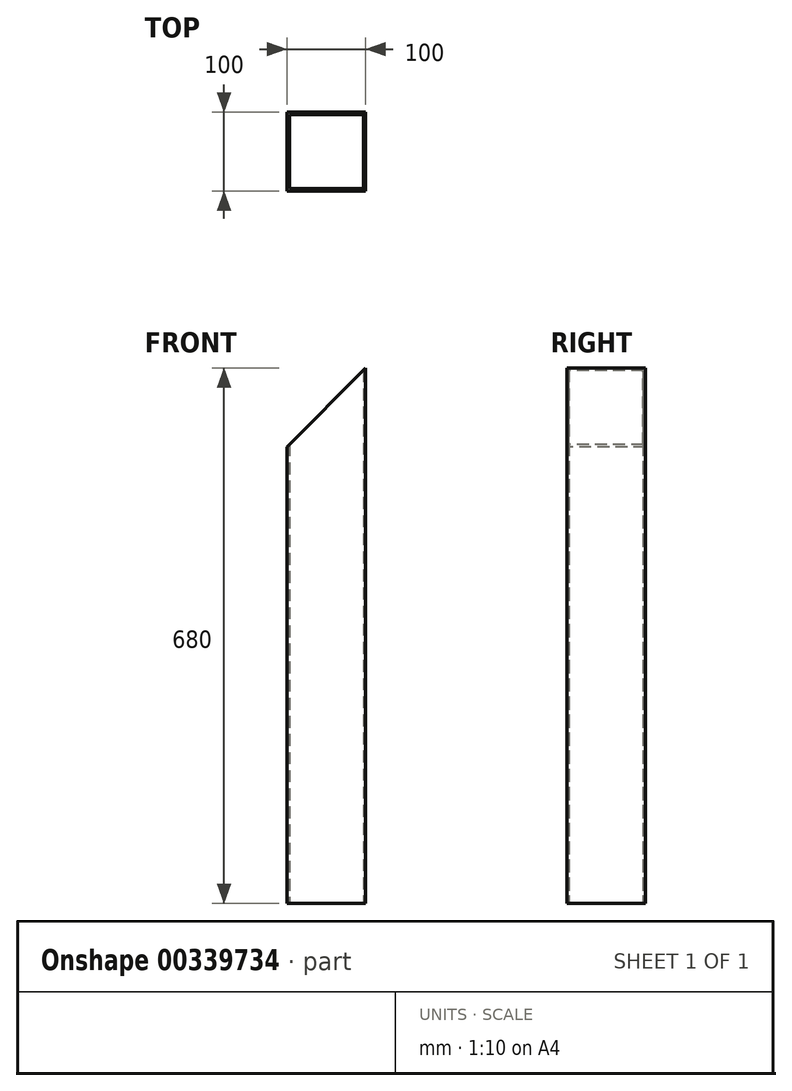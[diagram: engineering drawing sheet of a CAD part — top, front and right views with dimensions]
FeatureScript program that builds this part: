
annotation { "Feature Type Name" : "Feature", "Feature Type Description" : "" }
export const myFeature = defineFeature(function(context is Context, id is Id, definition is map)
    precondition{}
    {
        {
            var Q0;
            Q0=qCreatedBy(makeId("Top.planeOp"),FACE);
            var sketch = newSketch(context, id + "F0", { "sketchPlane" : qUnion([Q0])});
            skLineSegment(sketch, "E0.bottom", {"start": v(-44.84, 54.44) * mm, "end": v(55.16, 54.44) * mm});
            skLineSegment(sketch, "E0.top", {"start": v(-44.84, -45.56) * mm, "end": v(55.16, -45.56) * mm});
            skLineSegment(sketch, "E0.left", {"start": v(-44.84, 54.44) * mm, "end": v(-44.84, -45.56) * mm});
            skLineSegment(sketch, "E0.right", {"start": v(55.16, 54.44) * mm, "end": v(55.16, -45.56) * mm});
            skLineSegment(sketch, "E1.bottom", {"start": v(-41.84, 51.44) * mm, "end": v(52.16, 51.44) * mm});
            skLineSegment(sketch, "E1.top", {"start": v(-41.84, -42.56) * mm, "end": v(52.16, -42.56) * mm});
            skLineSegment(sketch, "E1.left", {"start": v(-41.84, 51.44) * mm, "end": v(-41.84, -42.56) * mm});
            skLineSegment(sketch, "E1.right", {"start": v(52.16, 51.44) * mm, "end": v(52.16, -42.56) * mm});
            skSolve(sketch);
        }
        {
            var Q0;
            Q0 = qSketchRegion(id + "F0", true);
            extrude(context, id + "F1", {"entities" : qUnion([Q0]), "depth" : 680 * mm});
        }
        {
            var Q0;
            Q0=makeQuery(id+"F1.opExtrude","SWEPT_FACE",FACE,{"disambiguationData":[OSD([sQuery(id+"F0.wireOp",EDGE,"E0.top")])]});
            var sketch = newSketch(context, id + "F2", { "sketchPlane" : qUnion([Q0])});
            skLineSegment(sketch, "E2", {"start": v(55.16, 680) * mm, "end": v(-155.7, 469.14) * mm});
            skSolve(sketch);
        }
        {
            var Q0;
            {var subQ1=sQuery(id+"F0.wireOp",EDGE,"E0.top");var subQ2=makeQuery(id+"F1.opExtrude","CAP_EDGE",EDGE,{"disambiguationData":[OSD([subQ1])],"isStart":false});Q0=makeQuery(id+"F2.imprint","IMPRINT",FACE,{"disambiguationData":[TD([[makeQuery(id+"F2.imprint","IMPRINT",EDGE,{"derivedFrom":subQ2}),-1.0]])]});}
            extrude(context, id + "F3", {"entities" : qUnion([Q0]), "operationType" : NewBodyOperationType.REMOVE, "oppositeDirection" : true, "depth" : 110 * mm});
        }
    });
